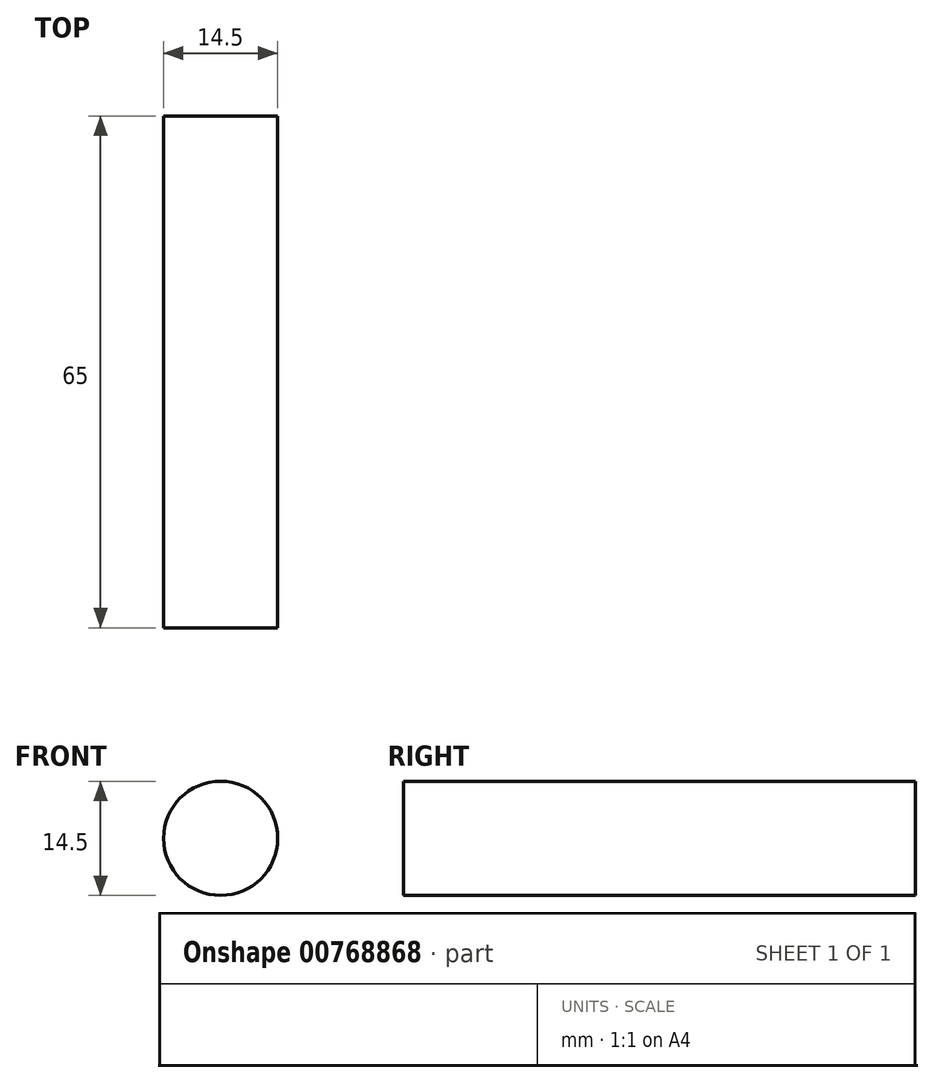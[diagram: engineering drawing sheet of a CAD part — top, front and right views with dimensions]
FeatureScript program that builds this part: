
annotation { "Feature Type Name" : "Feature", "Feature Type Description" : "" }
export const myFeature = defineFeature(function(context is Context, id is Id, definition is map)
    precondition{}
    {
        {
            var Q0;
            Q0=qCreatedBy(makeId("Front.planeOp"),FACE);
            var sketch = newSketch(context, id + "F0", { "sketchPlane" : qUnion([Q0])});
            skCircle(sketch, "E0", {"center": v(0, 0) * mm, "radius": 7.25 * mm});
            skSolve(sketch);
        }
        {
            var Q0;
            Q0 = qSketchRegion(id + "F0", true);
            extrude(context, id + "F1", {"entities" : qUnion([Q0]), "depth" : 65 * mm, "offsetDistance" : 25 * mm});
        }
    });
